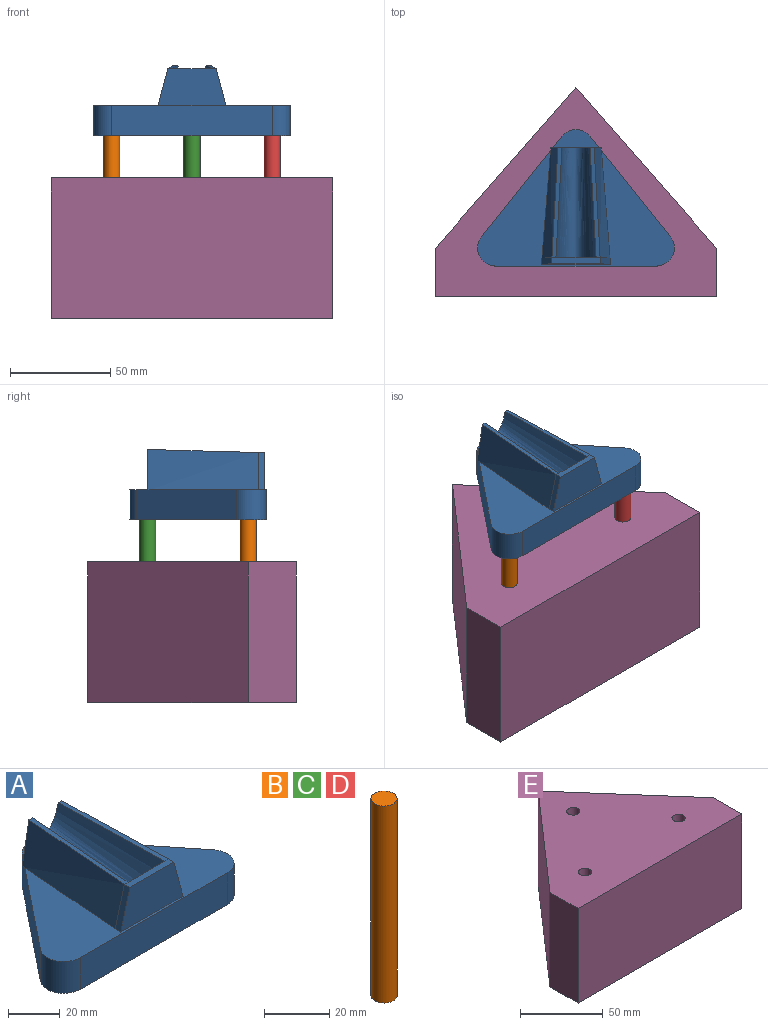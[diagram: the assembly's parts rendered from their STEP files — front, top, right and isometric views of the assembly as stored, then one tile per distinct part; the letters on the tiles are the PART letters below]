
ASSEMBLY  parts=5 mates=4
PART A: 28 faces, bbox 98x68x35 mm
  f0: plane 23.05x9mm, normal (0,0,1), area 137.4mm2, adj f1,f2,f3,f16
  f1: plane 50x40mm, normal (0.78,0.62,0), area 960.5mm2, adj f0,f2,f6,f7,f8,f15
  f2: cylinder r=9mm len=15mm, axis (0,0,-1), area 241.9mm2, adj f0,f1,f3,f8
  f3: plane 50x40mm, normal (-0.78,0.62,0), area 960.5mm2, adj f0,f2,f4,f7,f8,f22
  f4: cylinder r=9mm len=15mm, axis (0,0,-1), area 303.1mm2, adj f3,f5,f7,f8
  f5: plane 80x15mm, normal (0,-1,0), area 1200mm2, adj f4,f6,f7,f8
  f6: cylinder r=9mm len=15mm, axis (0,0,-1), area 303.1mm2, adj f1,f5,f7,f8
  f7: plane 98x57.61mm, normal (0,0,1), area 2267.7mm2, adj f1,f3,f4,f5,f6,f17,f21,f24
  f8: plane 98x68mm, normal (0,0,-1), area 3976.2mm2, adj f1,f2,f3,f4,f5,f6,f9,f11
  f9: cylinder r=4mm len=8mm, axis (0,0,-1), area 175.9mm2, adj f8,f10
  f10: plane 8x8mm, normal (0,0,-1), area 50.3mm2, adj f9
  f11: cylinder r=4mm len=8mm, axis (0,0,-1), area 175.9mm2, adj f8,f12
  f12: plane 8x8mm, normal (0,0,-1), area 50.3mm2, adj f11
  f13: cylinder r=4mm len=8mm, axis (0,0,-1), area 175.9mm2, adj f8,f14
  f14: plane 8x8mm, normal (0,0,-1), area 50.3mm2, adj f13
  f15: plane 1.39x1.11mm, normal (0,0,-1), area 0.7mm2, adj f1,f16,f17
  f16: plane 25.05x20mm, normal (0,1,0), area 329.4mm2, adj f0,f15,f17,f18,f19,f20,f21,f22
  f17: bspline ~55x20mm, area 1086.7mm2, adj f7,f15,f16,f18,f24
  f18: plane 55x5mm, normal (0,-0.03,1), area 110mm2, adj f16,f17,f19,f25
  f19: bspline ~55x20mm, area 1910.5mm2, adj f16,f18,f20,f23
  f20: plane 55x5mm, normal (0,-0.03,1), area 110mm2, adj f16,f19,f21,f25
  f21: bspline ~55x20mm, area 1086.7mm2, adj f7,f16,f20,f22,f26
  f22: plane 1.39x1.11mm, normal (0,0,-1), area 0.7mm2, adj f3,f16,f21
  f23: plane 20x18.91mm, normal (0,1,0), area 247.2mm2, adj f19,f25
  f24: plane 18.5x4.96mm, normal (0.97,0,0.26), area 57.5mm2, adj f7,f17,f25,f27
  f25: plane 24x3mm, normal (0,0,1), area 72mm2, adj f18,f20,f23,f24,f26,f27
  f26: plane 18.5x4.96mm, normal (-0.97,0,0.26), area 57.5mm2, adj f7,f21,f25,f27
  f27: plane 33.91x18.5mm, normal (0,-1,0), area 535.7mm2, adj f7,f24,f25,f26
PART B: 3 faces, bbox 8x8x74 mm
  f0: cylinder r=4mm len=74mm, axis (0,0,-1), area 1859.8mm2, adj f1,f2
  f1: plane 8x8mm, normal (0,0,1), area 50.3mm2, adj f0
  f2: plane 8x8mm, normal (0,0,-1), area 50.3mm2, adj f0
PART C: same geometry as B
PART D: same geometry as B
PART E: 10 faces, bbox 140x104x70 mm
  f0: plane 80x70mm, normal (0.75,0.66,0), area 7441.1mm2, adj f1,f5,f8,f9
  f1: plane 80x70mm, normal (-0.75,0.66,0), area 7441.1mm2, adj f0,f2,f8,f9
  f2: plane 70x24mm, normal (-1,0,0), area 1680mm2, adj f1,f3,f8,f9
  f3: plane 140x70mm, normal (0,-1,0), area 9800mm2, adj f2,f5,f8,f9
  f4: cylinder r=4mm len=70mm, axis (0,0,1), area 1759.3mm2, adj f8,f9
  f5: plane 70x24mm, normal (1,0,0), area 1680mm2, adj f0,f3,f8,f9
  f6: cylinder r=4mm len=70mm, axis (0,0,1), area 1759.3mm2, adj f8,f9
  f7: cylinder r=4mm len=70mm, axis (0,0,1), area 1759.3mm2, adj f8,f9
  f8: plane 140x104mm, normal (0,0,-1), area 8809.2mm2, adj f0,f1,f2,f3,f4,f5,f6,f7
  f9: plane 140x104mm, normal (0,0,1), area 8809.2mm2, adj f0,f1,f2,f3,f4,f5,f6,f7
PLACE A t=(43.27,102.92,4.23)mm
PLACE B t=(3.27,52.92,-38.77)mm
PLACE C t=(43.27,102.92,-38.77)mm
PLACE D t=(83.27,52.92,-38.77)mm
PLACE E t=(43.27,102.92,-16.77)mm fixed
MATE slider C.f0 <-> E.f6  axis (0,0,-1) through (43.27,102.92,-62.77)mm
MATE fastened D.f0 <-> A.f6  axis (0,0,1) through (83.27,52.92,11.23)mm
MATE fastened C.f0 <-> A.f9  axis (0,0,1) through (43.27,102.92,11.23)mm
MATE fastened B.f0 <-> A.f4  axis (0,0,1) through (3.27,52.92,11.23)mm
